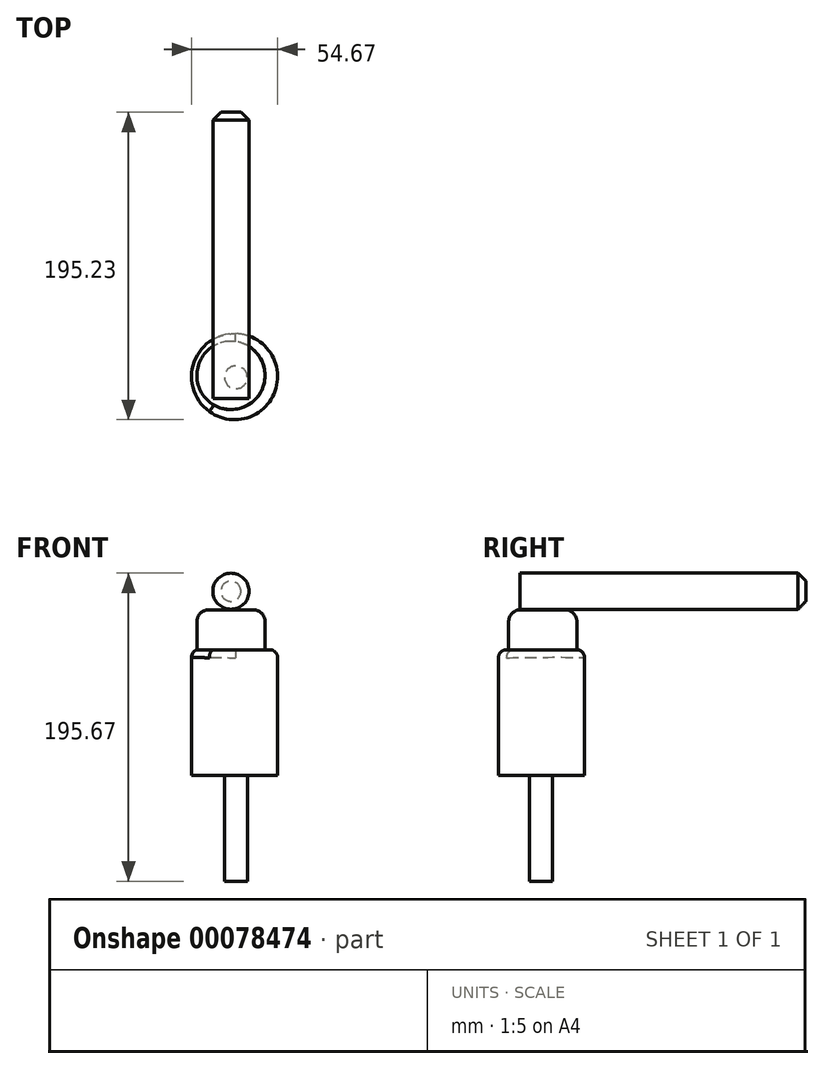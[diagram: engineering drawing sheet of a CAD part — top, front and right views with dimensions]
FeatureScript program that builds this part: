
annotation { "Feature Type Name" : "Feature", "Feature Type Description" : "" }
export const myFeature = defineFeature(function(context is Context, id is Id, definition is map)
    precondition{}
    {
        {
            var Q0;
            Q0=qCreatedBy(makeId("Top.planeOp"),FACE);
            var sketch = newSketch(context, id + "F0", { "sketchPlane" : qUnion([Q0])});
            skCircle(sketch, "E0", {"center": v(-36.44, 18) * mm, "radius": 27.34 * mm});
            skSolve(sketch);
        }
        {
            var Q0;
            Q0 = qSketchRegion(id + "F0", true);
            extrude(context, id + "F1", {"entities" : qUnion([Q0]), "depth" : 79.84 * mm});
        }
        {
            var Q0;
            Q0=makeQuery(id+"F1.opExtrude","CAP_FACE",FACE,{"disambiguationData":[OSD([sQuery(id+"F0.wireOp",EDGE,"E0")])],"isStart":false});
            var sketch = newSketch(context, id + "F2", { "sketchPlane" : qUnion([Q0])});
            skCircle(sketch, "E1", {"center": v(-38.74, 18.77) * mm, "radius": 21.67 * mm});
            skSolve(sketch);
        }
        {
            var Q0;
            Q0 = qSketchRegion(id + "F2", true);
            extrude(context, id + "F3", {"entities" : qUnion([Q0]), "operationType" : NewBodyOperationType.ADD, "depth" : 25.4 * mm});
        }
        {
            var Q0;
            Q0=makeQuery(id+"F3.opExtrude","CAP_FACE",FACE,{"disambiguationData":[OSD([sQuery(id+"F2.wireOp",EDGE,"E1")])],"isStart":false});
            var sketch = newSketch(context, id + "F4", { "sketchPlane" : qUnion([Q0])});
            skLineSegment(sketch, "E2", {"start": v(-54.8, 4.23) * mm, "end": v(-22.67, 4.23) * mm});
            skSolve(sketch);
        }
        {
            var Q0;
            Q0=sQuery(id+"F4.wireOp",EDGE,"E2");
            extrude(context, id + "F5", {"bodyType" : ToolBodyType.SURFACE, "surfaceEntities" : qUnion([Q0]), "depth" : 25.4 * mm});
        }
        {
            var Q0;
            Q0=makeQuery(id+"F5.opExtrude","SWEPT_FACE",FACE,{"disambiguationData":[OSD([sQuery(id+"F4.wireOp",EDGE,"E2")])]});
            var sketch = newSketch(context, id + "F6", { "sketchPlane" : qUnion([Q0])});
            skCircle(sketch, "E3", {"center": v(-38.77, 116.97) * mm, "radius": 11.47 * mm});
            skSolve(sketch);
        }
        {
            var Q0;
            Q0 = qSketchRegion(id + "F6", true);
            extrude(context, id + "F7", {"entities" : qUnion([Q0]), "oppositeDirection" : true, "depth" : 181.65 * mm});
        }
        {
            var Q0;
            Q0=makeQuery(id+"F1.opExtrude","CAP_FACE",FACE,{"disambiguationData":[OSD([sQuery(id+"F0.wireOp",EDGE,"E0")])],"isStart":true});
            var sketch = newSketch(context, id + "F8", { "sketchPlane" : qUnion([Q0])});
            skCircle(sketch, "E4", {"center": v(-35.62, -17.57) * mm, "radius": 7.27 * mm});
            skSolve(sketch);
        }
        {
            var Q0;
            Q0 = qSketchRegion(id + "F8", true);
            extrude(context, id + "F9", {"entities" : qUnion([Q0]), "operationType" : NewBodyOperationType.ADD, "depth" : 67.23 * mm});
        }
        {
            var Q0;
            Q0=makeQuery(id+"F1.opExtrude","CAP_EDGE",EDGE,{"disambiguationData":[OSD([sQuery(id+"F0.wireOp",EDGE,"E0")])],"isStart":false});
            fillet(context, id + "F10", {"entities" : qUnion([Q0]), "radius" : 5.08 * mm, "tangentPropagation" : true, "allowEdgeOverflow" : false});
        }
        {
            var Q0;
            Q0=makeQuery(id+"F3.opExtrude","CAP_EDGE",EDGE,{"disambiguationData":[OSD([sQuery(id+"F2.wireOp",EDGE,"E1")])],"isStart":false});
            fillet(context, id + "F11", {"entities" : qUnion([Q0]), "radius" : 7.62 * mm, "tangentPropagation" : true, "allowEdgeOverflow" : false});
        }
        {
            var Q0;
            Q0=makeQuery(id+"F7.opExtrude","CAP_EDGE",EDGE,{"disambiguationData":[OSD([sQuery(id+"F6.wireOp",EDGE,"E3")])],"isStart":false});
            chamfer(context, id + "F12", {"entities" : qUnion([Q0]), "width" : 5.08 * mm, "tangentPropagation" : true});
        }
    });
